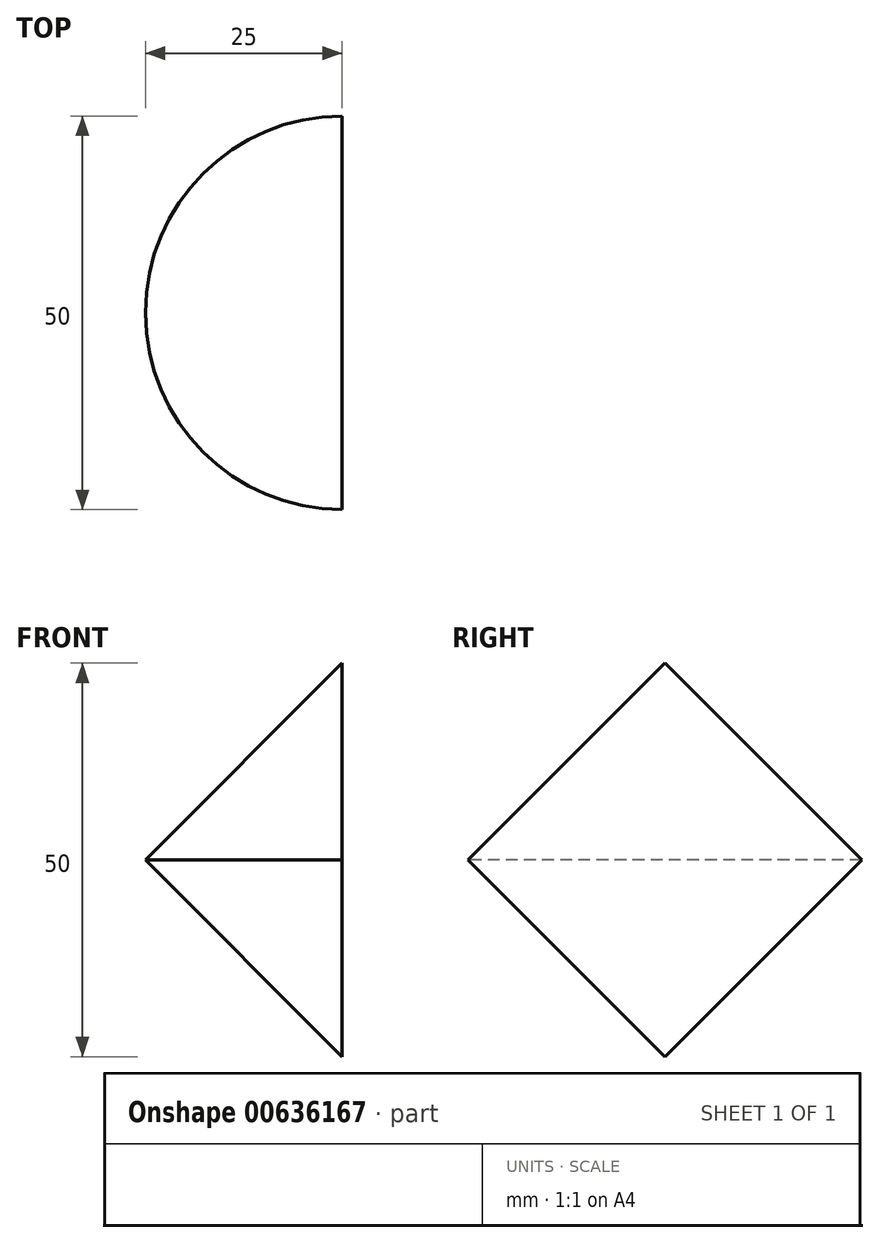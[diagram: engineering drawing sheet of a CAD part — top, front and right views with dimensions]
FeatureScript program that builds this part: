
annotation { "Feature Type Name" : "Feature", "Feature Type Description" : "" }
export const myFeature = defineFeature(function(context is Context, id is Id, definition is map)
    precondition{}
    {
        {
            var Q0;
            Q0=qCreatedBy(makeId("Top.planeOp"),FACE);
            var sketch = newSketch(context, id + "F0", { "sketchPlane" : qUnion([Q0])});
            skCircle(sketch, "E0", {"center": v(0, 0) * mm, "radius": 25 * mm});
            skSolve(sketch);
        }
        {
            var Q0;
            Q0 = qSketchRegion(id + "F0", true);
            extrude(context, id + "F1", {"entities" : qUnion([Q0]), "endBound" : BoundingType.SYMMETRIC, "depth" : 50 * mm, "offsetDistance" : 25 * mm});
        }
        {
            var Q0;
            Q0=makeQuery(id+"F1.opExtrude","CAP_EDGE",EDGE,{"disambiguationData":[OSD([sQuery(id+"F0.wireOp",EDGE,"E0")])],"isStart":false});
            var Q1;
            Q1=makeQuery(id+"F1.opExtrude","CAP_EDGE",EDGE,{"disambiguationData":[OSD([sQuery(id+"F0.wireOp",EDGE,"E0")])],"isStart":true});
            chamfer(context, id + "F2", {"entities" : qUnion([Q0, Q1]), "chamferType" : ChamferType.TWO_OFFSETS, "width1" : 25 * mm, "oppositeDirection" : false, "width2" : 25 * mm, "tangentPropagation" : true});
        }
        {
            var Q0;
            Q0=qCreatedBy(makeId("Right.planeOp"),FACE);
            var sketch = newSketch(context, id + "F3", { "sketchPlane" : qUnion([Q0])});
            skLineSegment(sketch, "E1.bottom", {"start": v(-27.5, 27.5) * mm, "end": v(27.5, 27.5) * mm});
            skLineSegment(sketch, "E1.top", {"start": v(-27.5, -27.5) * mm, "end": v(27.5, -27.5) * mm});
            skLineSegment(sketch, "E1.left", {"start": v(-27.5, 27.5) * mm, "end": v(-27.5, -27.5) * mm});
            skLineSegment(sketch, "E1.right", {"start": v(27.5, 27.5) * mm, "end": v(27.5, -27.5) * mm});
            skPoint(sketch, "E1.middle", {"position": v(0, 0) * mm});
            skSolve(sketch);
        }
        {
            var Q0;
            Q0=makeQuery(id+"F3.imprint","IMPRINT",FACE,{"disambiguationData":[TD([[makeQuery(id+"F3.imprint","IMPRINT",EDGE,{"derivedFrom":sQuery(id+"F3.wireOp",EDGE,"E1.bottom")}),-1.0]])]});
            extrude(context, id + "F4", {"entities" : qUnion([Q0]), "operationType" : NewBodyOperationType.REMOVE, "depth" : 30 * mm, "offsetDistance" : 25 * mm});
        }
    });
